# Revit family: 10.5 Inch Sill -S385
name_source: partatom
category: Generic Models
units: mm (PartAtom-declared; Revit-internal decimal feet)

## family parameters
Always vertical = Yes
Can host rebar = No
Cut with Voids When Loaded = No
Part Type = Normal
Room Calculation Point = No
Round Connector Dimension = Use Diameter
Shared = No
Work Plane-Based = No

## types (1)
- 10.5 Inch Sill -S385
    Construction Type = Precast
    Default Elevation = 0 mm  [stored 0 ft]
    Description = Type 10½ Inch-Sill
    Detailing = As per design specification and product drawings.
    Distance from Face to Seating = 212 mm  [stored 0.695538 ft]
    Front Face Dimension = 45 mm  [stored 0.147638 ft]
    Keynote = The information contained is the sole property of KPC Ltd., any reproduction in part or whole without permission of KPC Ltd. is prohibited.
    Length Options = Stock sizes 552mm, 665mm, 777mm, 890mm, 1002mm, 1050mm, 1115mm, 1227mm, 1340mm, 1452mm, 1565mm, 1677mm, 1790mm, 1902mm, 2015mm, 2127mm, 2240mm, 2352mm, 2465mm, 2577mm, 2690mm, 2802mm, 2915mm
    Load Bearing = No
    Manufacturer = Killeshal Precast Concrete Ltd.
    Model = S/385 Sill
    Service Life = 0.000000
    Shape = As per drawing
    Size = 267mm x 100 to 45mm
    Slope = 0.00°
    Span = Ope Size + 205mm overhang.
    Type Comments = Visit our website for a full list of available products.
    Types = Single
    URL = www.killeshal.com
    Weight = 44Kg/m
    Width of Seating = 55 mm  [stored 0.180446 ft]

note: [stored X ft] marks values corroborated as IEEE doubles in the binary element streams (Revit-internal decimal feet)

## geometry (parser evidence)
native form markers: Sweep x3
no freeform markers — native parametric forms only
